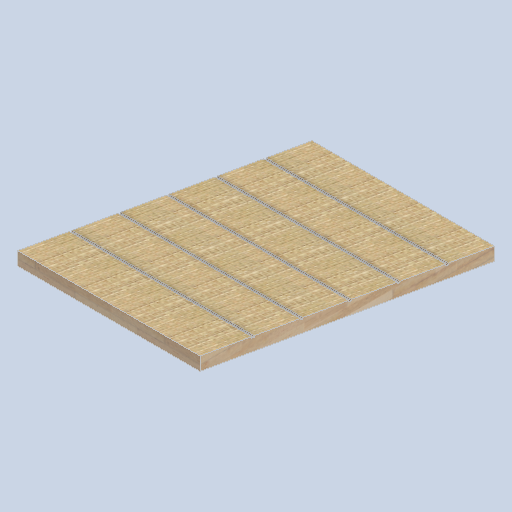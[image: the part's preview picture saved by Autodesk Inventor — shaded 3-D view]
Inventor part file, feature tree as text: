
AUTODESK INVENTOR PART (.ipt)
format: ipt  version: 2024.2 (Build 282272000, 272)  size: 257,024 bytes
history: native  units: in
note: dims shown in document units (in); Inventor stores cm internally (conversion verified against a paired STEP export)
features: sketch x5, other x3, plane x3
ambient origin geometry x8: Origin, YZ Plane, XZ Plane, XY Plane, X Axis, Y Axis, Z Axis, Center Point
bodies: Solid1 (feature_tree)
feature tree (11):
  other  "eave_panel_01.ipt"
  other  "Solid1::eave_panel_01.ipt"
  other  "TaggingFeature1"
  sketch  "Sketch1"  dims[d0=0.3937in]
  sketch  "Sketch2"
  sketch  "Sketch3"
  sketch  "Sketch4"
  sketch  "Sketch5"
  plane  "Work Plane1"
  plane  "Work Plane2"
  plane  "Work Plane3"
